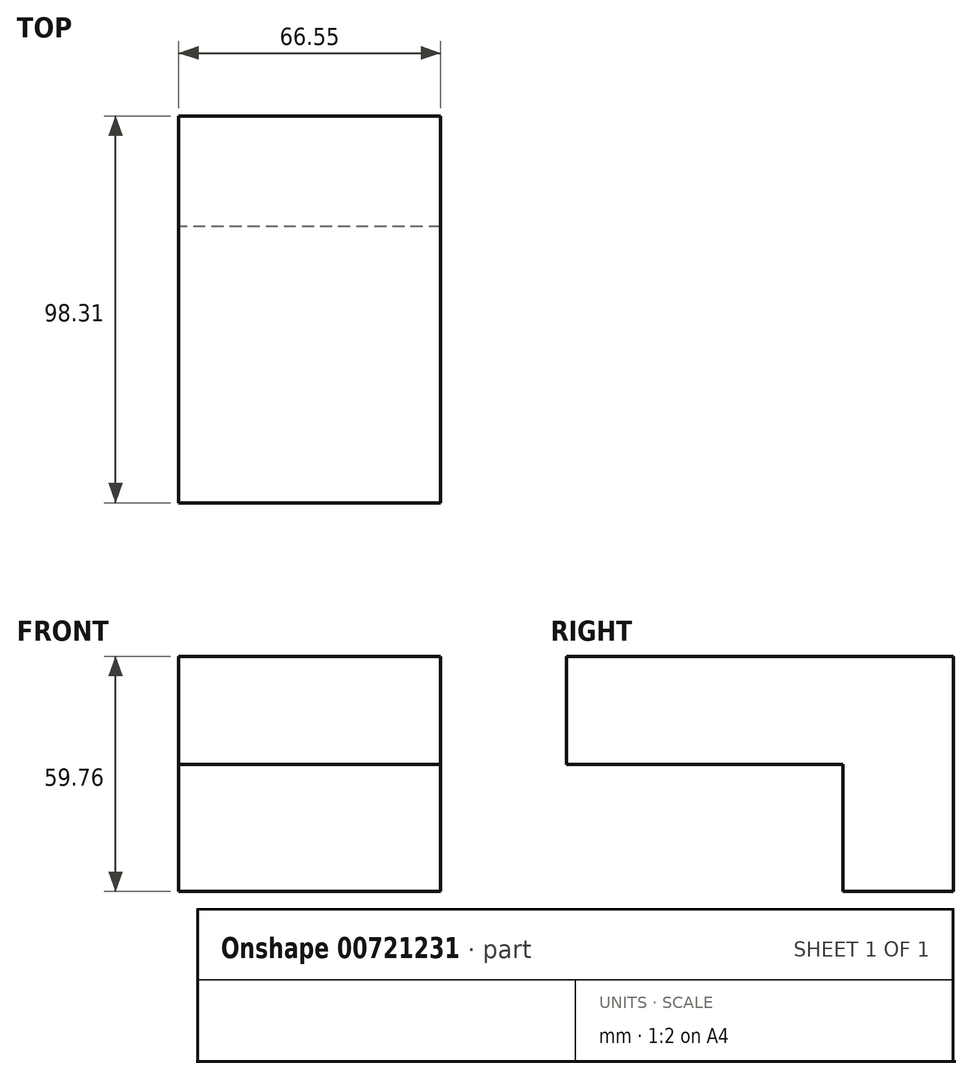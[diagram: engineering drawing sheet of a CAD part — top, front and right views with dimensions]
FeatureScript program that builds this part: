
annotation { "Feature Type Name" : "Feature", "Feature Type Description" : "" }
export const myFeature = defineFeature(function(context is Context, id is Id, definition is map)
    precondition{}
    {
        {
            var Q0;
            Q0=qCreatedBy(makeId("Right.planeOp"),FACE);
            var sketch = newSketch(context, id + "F0", { "sketchPlane" : qUnion([Q0])});
            skLineSegment(sketch, "E0.bottom", {"start": v(-98.3, -13.75) * mm, "end": v(70.24, -13.75) * mm});
            skLineSegment(sketch, "E0.top", {"start": v(-69.44, 13.75) * mm, "end": v(98.3, 13.75) * mm});
            skLineSegment(sketch, "E0.left", {"start": v(-98.3, -13.75) * mm, "end": v(-98.3, 13.75) * mm});
            skLineSegment(sketch, "E0.right", {"start": v(98.3, -13.75) * mm, "end": v(98.3, 13.75) * mm});
            skPoint(sketch, "E0.middle", {"position": v(0, 0) * mm});
            skLineSegment(sketch, "E1.bottom", {"start": v(-98.3, 49.75) * mm, "end": v(-98.3, 49.75) * mm});
            skLineSegment(sketch, "E1.top", {"start": v(-98.3, -77.25) * mm, "end": v(-98.3, -77.25) * mm});
            skLineSegment(sketch, "E1.left", {"start": v(-98.3, 49.75) * mm, "end": v(-98.3, -13.75) * mm});
            skLineSegment(sketch, "E1.right", {"start": v(-98.3, 49.75) * mm, "end": v(-98.3, -13.75) * mm});
            skPoint(sketch, "E1.middle", {"position": v(-98.3, -13.75) * mm});
            skPoint(sketch, "E1.cornerSnap0", {"position": v(-98.3, 0) * mm});
            skLineSegment(sketch, "E2.bottom", {"start": v(-69.44, 49.75) * mm, "end": v(-98.3, 49.75) * mm});
            skLineSegment(sketch, "E2.top", {"start": v(-69.44, 49.75) * mm, "end": v(-98.3, 49.75) * mm});
            skLineSegment(sketch, "E2.left", {"start": v(-69.44, 49.75) * mm, "end": v(-69.44, 49.75) * mm});
            skLineSegment(sketch, "E2.right", {"start": v(-127.17, 49.75) * mm, "end": v(-127.17, 49.75) * mm});
            skPoint(sketch, "E2.middle", {"position": v(-98.3, 49.75) * mm});
            skLineSegment(sketch, "E3.top", {"start": v(-69.44, -22.24) * mm, "end": v(-69.44, -22.24) * mm});
            skLineSegment(sketch, "E3.left", {"start": v(-69.44, 49.75) * mm, "end": v(-69.44, 13.75) * mm});
            skLineSegment(sketch, "E3.right", {"start": v(-69.44, 49.75) * mm, "end": v(-69.44, 13.75) * mm});
            skPoint(sketch, "E3.middle", {"position": v(-69.44, 13.75) * mm});
            skLineSegment(sketch, "E4.bottom", {"start": v(98.3, 13.75) * mm, "end": v(98.3, 13.75) * mm});
            skLineSegment(sketch, "E4.top", {"start": v(98.3, 93.21) * mm, "end": v(98.3, 93.21) * mm});
            skPoint(sketch, "E4.middle", {"position": v(98.3, 53.48) * mm});
            skLineSegment(sketch, "E5.bottom", {"start": v(98.3, -13.75) * mm, "end": v(98.3, -13.75) * mm});
            skLineSegment(sketch, "E5.top", {"start": v(98.3, -78.27) * mm, "end": v(98.3, -78.27) * mm});
            skLineSegment(sketch, "E5.left", {"start": v(98.3, -13.75) * mm, "end": v(98.3, -46.01) * mm});
            skLineSegment(sketch, "E5.right", {"start": v(98.3, -13.75) * mm, "end": v(98.3, -46.01) * mm});
            skPoint(sketch, "E5.middle", {"position": v(98.3, -46.01) * mm});
            skLineSegment(sketch, "E6.bottom", {"start": v(98.3, -46.01) * mm, "end": v(70.24, -46.01) * mm});
            skLineSegment(sketch, "E6.top", {"start": v(98.3, -46.01) * mm, "end": v(70.24, -46.01) * mm});
            skLineSegment(sketch, "E6.left", {"start": v(98.3, -46.01) * mm, "end": v(98.3, -46.01) * mm});
            skLineSegment(sketch, "E6.right", {"start": v(24.28, -46.01) * mm, "end": v(24.28, -46.01) * mm});
            skPoint(sketch, "E6.middle", {"position": v(61.3, -46.01) * mm});
            skLineSegment(sketch, "E7.bottom", {"start": v(61.3, -46.01) * mm, "end": v(61.3, -46.01) * mm});
            skLineSegment(sketch, "E7.top", {"start": v(61.3, 18.5) * mm, "end": v(61.3, 18.5) * mm});
            skPoint(sketch, "E7.middle", {"position": v(61.3, -13.75) * mm});
            skLineSegment(sketch, "E8.0", {"start": v(70.24, -46.01) * mm, "end": v(70.24, -13.75) * mm});
            skLineSegment(sketch, "E9.bottom", {"start": v(0, 13.75) * mm, "end": v(0, 13.75) * mm});
            skLineSegment(sketch, "E9.top", {"start": v(0, -41.26) * mm, "end": v(0, -41.26) * mm});
            skLineSegment(sketch, "E9.left", {"start": v(0, 13.75) * mm, "end": v(0, -13.75) * mm});
            skLineSegment(sketch, "E9.right", {"start": v(0, 13.75) * mm, "end": v(0, -13.75) * mm});
            skPoint(sketch, "E9.middle", {"position": v(0, -13.75) * mm});
            skSolve(sketch);
        }
        {
            var Q0;
            {var subQ0=sQuery(id+"F0.wireOp",EDGE,"E2.top");Q0=makeQuery(id+"F0.imprint","IMPRINT",FACE,{"disambiguationData":[TD([[makeQuery(id+"F0.imprint","IMPRINT",EDGE,{"derivedFrom":subQ0}),1.0]])]});}
            var Q1;
            {var subQ0=sQuery(id+"F0.wireOp",EDGE,"E0.right");Q1=makeQuery(id+"F0.imprint","IMPRINT",FACE,{"disambiguationData":[TD([[makeQuery(id+"F0.imprint","IMPRINT",EDGE,{"derivedFrom":subQ0}),1.0]])]});}
            extrude(context, id + "F1", {"entities" : qUnion([Q0, Q1]), "depth" : 66.55 * mm, "offsetDistance" : 25.4 * mm});
        }
    });
